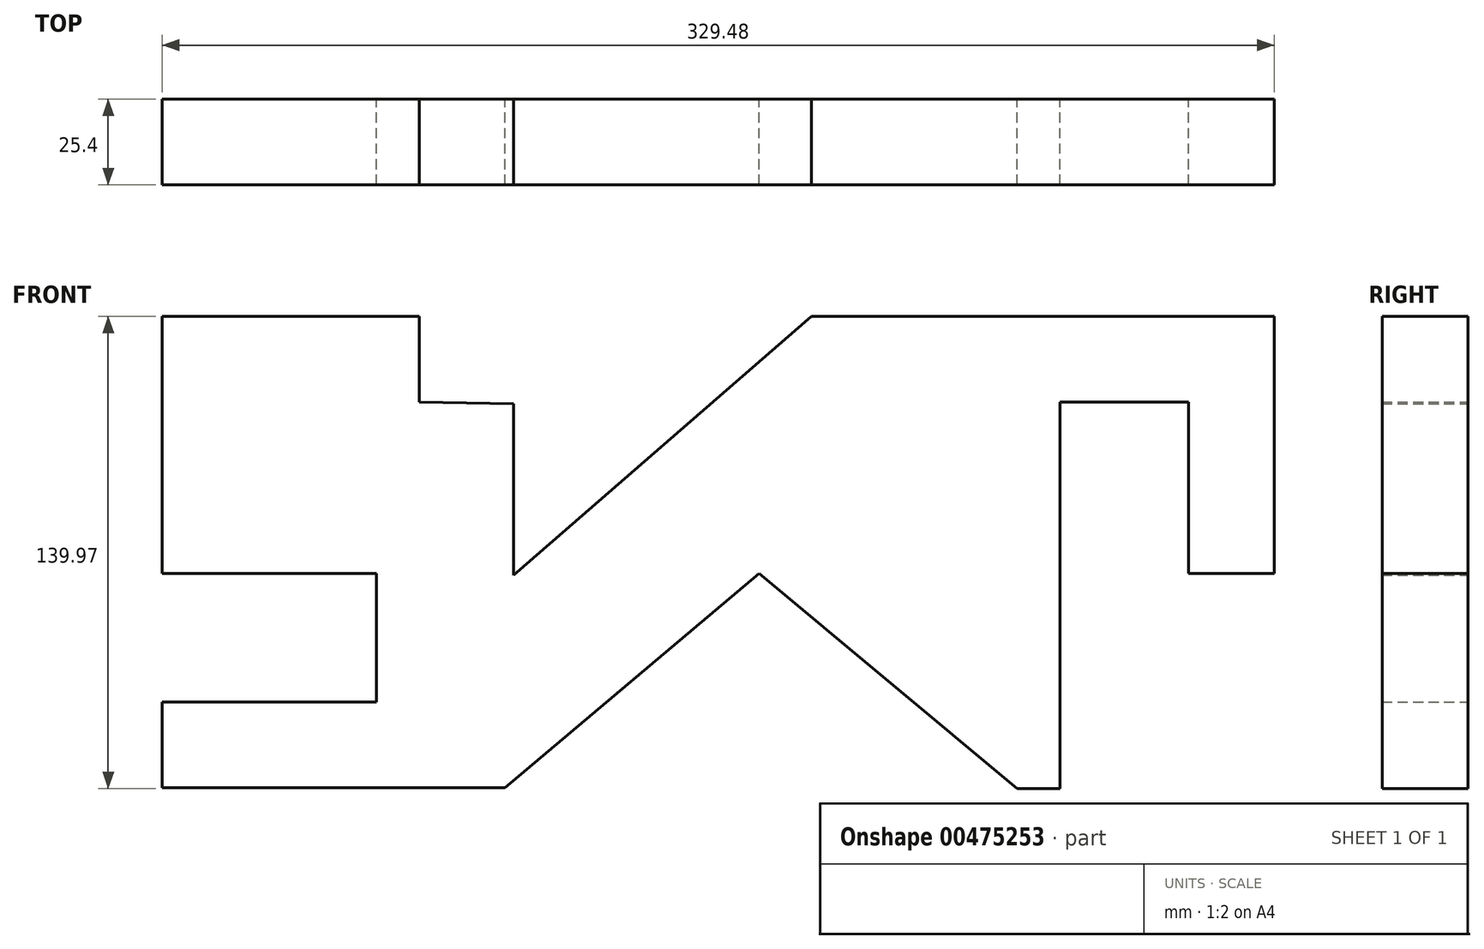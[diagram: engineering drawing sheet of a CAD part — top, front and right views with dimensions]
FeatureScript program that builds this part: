
annotation { "Feature Type Name" : "Feature", "Feature Type Description" : "" }
export const myFeature = defineFeature(function(context is Context, id is Id, definition is map)
    precondition{}
    {
        {
            var Q0;
            Q0=qCreatedBy(makeId("Front.planeOp"),FACE);
            var sketch = newSketch(context, id + "F0", { "sketchPlane" : qUnion([Q0])});
            skLineSegment(sketch, "E0", {"start": v(-95.14, 76.2) * mm, "end": v(-95.14, 0) * mm});
            skLineSegment(sketch, "E1", {"start": v(-95.14, 76.2) * mm, "end": v(-18.94, 76.2) * mm});
            skLineSegment(sketch, "E2", {"start": v(-18.94, 76.2) * mm, "end": v(-18.94, 50.8) * mm});
            skLineSegment(sketch, "E3", {"start": v(-18.94, 50.8) * mm, "end": v(9, 50.35) * mm});
            skLineSegment(sketch, "E4", {"start": v(9, 50.35) * mm, "end": v(9, -0.45) * mm});
            skLineSegment(sketch, "E5", {"start": v(9, -0.45) * mm, "end": v(97.18, 76.2) * mm});
            skLineSegment(sketch, "E6", {"start": v(97.18, 76.2) * mm, "end": v(234.34, 76.2) * mm});
            skLineSegment(sketch, "E7", {"start": v(-95.14, 0) * mm, "end": v(-31.64, 0) * mm});
            skLineSegment(sketch, "E8", {"start": v(-31.64, 0) * mm, "end": v(-31.64, -38.1) * mm});
            skLineSegment(sketch, "E9", {"start": v(-31.64, -38.1) * mm, "end": v(-95.14, -38.1) * mm});
            skLineSegment(sketch, "E10", {"start": v(-95.14, -38.1) * mm, "end": v(-95.14, -63.5) * mm});
            skLineSegment(sketch, "E11", {"start": v(-95.14, -63.5) * mm, "end": v(6.46, -63.5) * mm});
            skLineSegment(sketch, "E12", {"start": v(6.46, -63.5) * mm, "end": v(81.74, 0) * mm});
            skLineSegment(sketch, "E13", {"start": v(170.84, -63.77) * mm, "end": v(170.84, 50.8) * mm});
            skLineSegment(sketch, "E14", {"start": v(170.84, 50.8) * mm, "end": v(208.94, 50.8) * mm});
            skLineSegment(sketch, "E15", {"start": v(208.94, 50.8) * mm, "end": v(208.94, 0) * mm});
            skLineSegment(sketch, "E16", {"start": v(208.94, 0) * mm, "end": v(234.34, 0) * mm});
            skLineSegment(sketch, "E17", {"start": v(234.34, 0) * mm, "end": v(234.34, 76.2) * mm});
            skLineSegment(sketch, "E18", {"start": v(81.74, 0) * mm, "end": v(158.14, -63.77) * mm});
            skLineSegment(sketch, "E19", {"start": v(158.14, -63.77) * mm, "end": v(170.84, -63.77) * mm});
            skSolve(sketch);
        }
        {
            var Q0;
            Q0=makeQuery(id+"F0.imprint","IMPRINT",FACE,{"disambiguationData":[TD([[makeQuery(id+"F0.imprint","IMPRINT",EDGE,{"derivedFrom":sQuery(id+"F0.wireOp",EDGE,"E0")}),1.0]])]});
            extrude(context, id + "F1", {"entities" : qUnion([Q0]), "depth" : 25.4 * mm});
        }
    });
